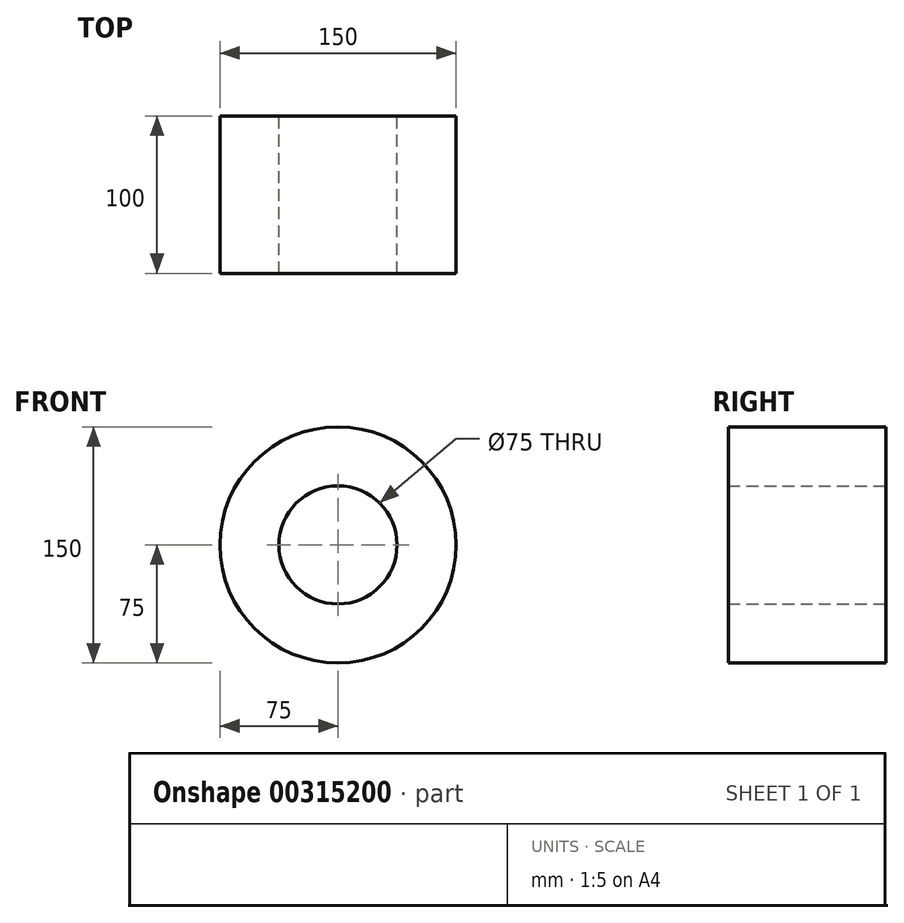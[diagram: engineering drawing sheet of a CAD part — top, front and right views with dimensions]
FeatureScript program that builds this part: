
annotation { "Feature Type Name" : "Feature", "Feature Type Description" : "" }
export const myFeature = defineFeature(function(context is Context, id is Id, definition is map)
    precondition{}
    {
        {
            var Q0;
            Q0=qCreatedBy(makeId("Front.planeOp"),FACE);
            var sketch = newSketch(context, id + "F0", { "sketchPlane" : qUnion([Q0])});
            skCircle(sketch, "E0", {"center": v(0, 0) * mm, "radius": 75 * mm});
            skSolve(sketch);
        }
        {
            var Q0;
            Q0=makeQuery(id+"F0.imprint","IMPRINT",FACE,{"disambiguationData":[TD([[makeQuery(id+"F0.imprint","IMPRINT",EDGE,{"derivedFrom":sQuery(id+"F0.wireOp",EDGE,"E0")}),1.0]])]});
            var sketch = newSketch(context, id + "F1", { "sketchPlane" : qUnion([Q0])});
            skCircle(sketch, "E1", {"center": v(0, 0) * mm, "radius": 37.5 * mm});
            skSolve(sketch);
        }
        {
            var Q0;
            Q0=makeQuery(id+"F0.imprint","IMPRINT",FACE,{"disambiguationData":[TD([[makeQuery(id+"F0.imprint","IMPRINT",EDGE,{"derivedFrom":sQuery(id+"F0.wireOp",EDGE,"E0")}),1.0]])]});
            extrude(context, id + "F2", {"entities" : qUnion([Q0]), "depth" : 100 * mm});
        }
        {
            var Q0;
            Q0=makeQuery(id+"F1.imprint","IMPRINT",FACE,{"disambiguationData":[TD([[makeQuery(id+"F1.imprint","IMPRINT",EDGE,{"derivedFrom":sQuery(id+"F1.wireOp",EDGE,"E1")}),1.0]])]});
            extrude(context, id + "F3", {"entities" : qUnion([Q0]), "operationType" : NewBodyOperationType.REMOVE, "endBound" : BoundingType.THROUGH_ALL, "depth" : 100 * mm});
        }
    });
